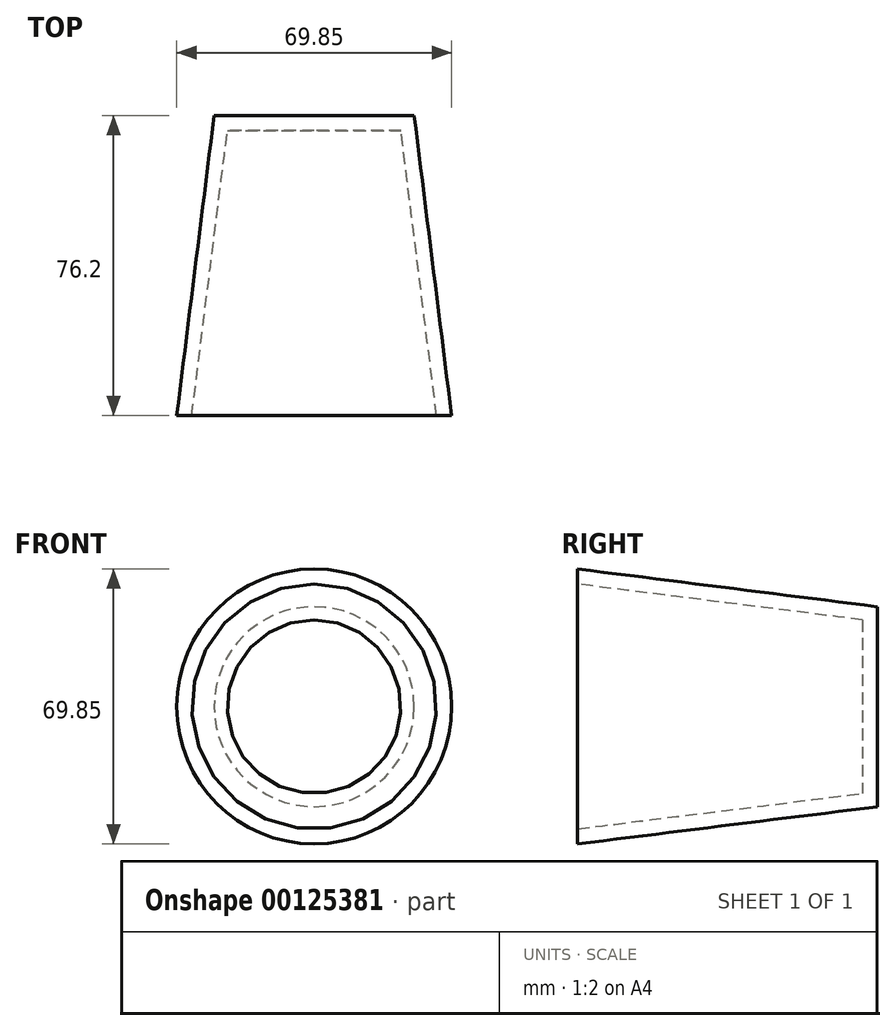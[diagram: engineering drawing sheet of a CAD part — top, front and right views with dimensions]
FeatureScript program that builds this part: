
annotation { "Feature Type Name" : "Feature", "Feature Type Description" : "" }
export const myFeature = defineFeature(function(context is Context, id is Id, definition is map)
    precondition{}
    {
        {
            var Q0;
            Q0=qCreatedBy(makeId("Front.planeOp"),FACE);
            var sketch = newSketch(context, id + "F0", { "sketchPlane" : qUnion([Q0])});
            skCircle(sketch, "E0", {"center": v(-4.56, 5.28) * mm, "radius": 25.4 * mm});
            skSolve(sketch);
        }
        {
            var Q0;
            Q0=makeQuery(id+"F0.imprint","IMPRINT",FACE,{"disambiguationData":[TD([[makeQuery(id+"F0.imprint","IMPRINT",EDGE,{"derivedFrom":sQuery(id+"F0.wireOp",EDGE,"E0")}),1.0]])]});
            cPlane(context, id + "F1", {"entities" : qUnion([Q0]), "cplaneType" : CPlaneType.OFFSET, "offset" : 76.2 * mm, "width" : 152.4 * mm, "height" : 152.4 * mm});
        }
        {
            var Q0;
            Q0=qCreatedBy(id+"F1.planeOp",FACE);
            var sketch = newSketch(context, id + "F2", { "sketchPlane" : qUnion([Q0])});
            skCircle(sketch, "E1", {"center": v(-4.56, 5.34) * mm, "radius": 34.93 * mm});
            skSolve(sketch);
        }
        {
            var Q0;
            Q0=makeQuery(id+"F0.imprint","IMPRINT",FACE,{"disambiguationData":[TD([[makeQuery(id+"F0.imprint","IMPRINT",EDGE,{"derivedFrom":sQuery(id+"F0.wireOp",EDGE,"E0")}),1.0]])]});
            var Q1;
            Q1=makeQuery(id+"F2.imprint","IMPRINT",FACE,{"disambiguationData":[TD([[makeQuery(id+"F2.imprint","IMPRINT",EDGE,{"derivedFrom":sQuery(id+"F2.wireOp",EDGE,"E1")}),1.0]])]});
            loft(context, id + "F3", {"sheetProfilesArray" : [{ "sheetProfileEntities" : qUnion([Q0]) }, { "sheetProfileEntities" : qUnion([Q1]) }]});
        }
        {
            var Q0;
            Q0=makeQuery(id+"F3.opLoft","CAP_FACE",FACE,{"disambiguationData":[OSD([makeQuery(id+"F2.imprint","IMPRINT",FACE,{"disambiguationData":[TD([[makeQuery(id+"F2.imprint","IMPRINT",EDGE,{"derivedFrom":sQuery(id+"F2.wireOp",EDGE,"E1")}),1.0]])]})])],"isStart":true});
            shell(context, id + "F4", {"entities" : qUnion([Q0]), "thickness" : 3.8 * mm});
        }
    });
